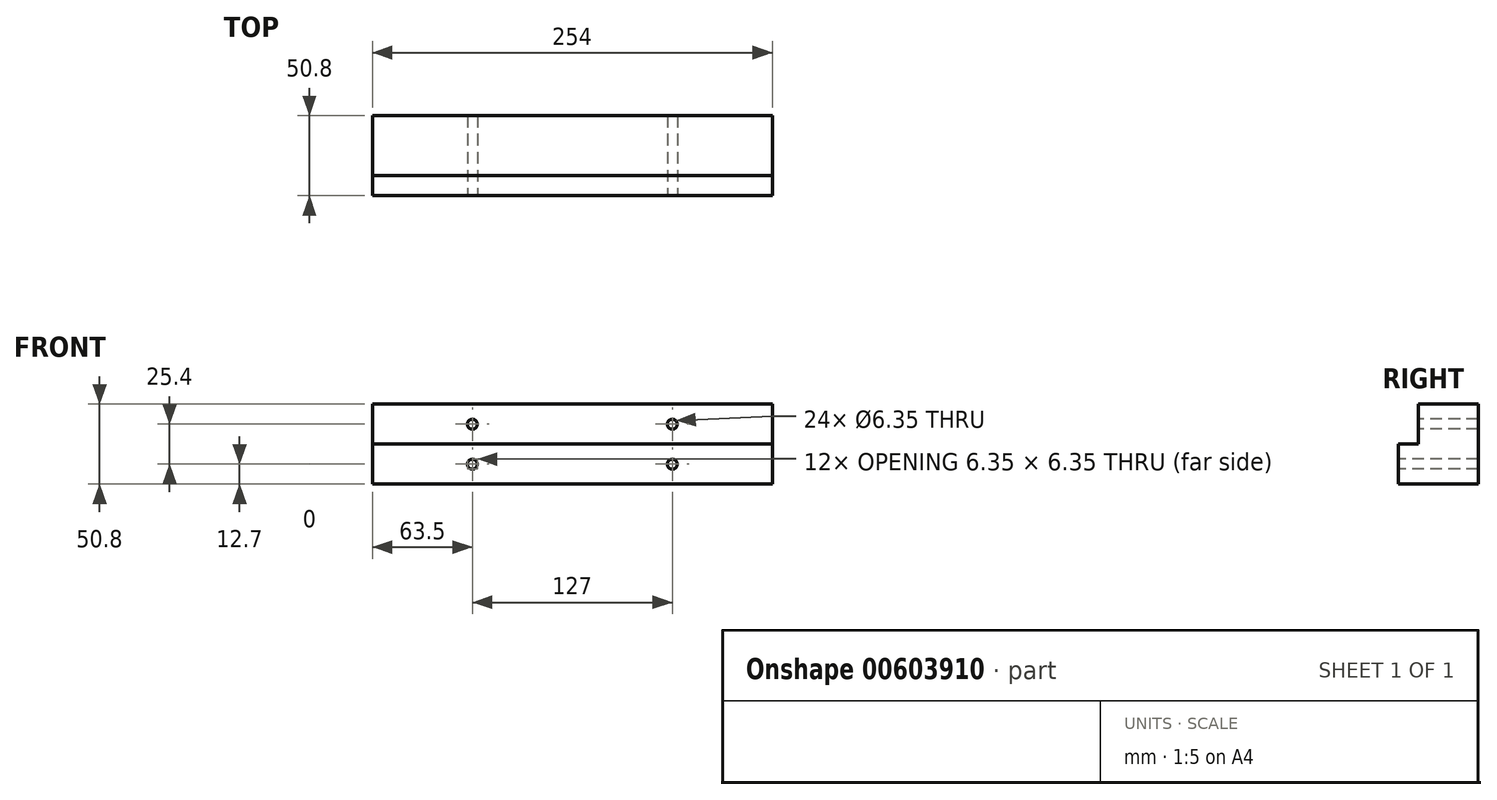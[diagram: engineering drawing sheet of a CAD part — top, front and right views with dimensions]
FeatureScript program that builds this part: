
annotation { "Feature Type Name" : "Feature", "Feature Type Description" : "" }
export const myFeature = defineFeature(function(context is Context, id is Id, definition is map)
    precondition{}
    {
        {
            var Q0;
            Q0=qCreatedBy(makeId("Right.planeOp"),FACE);
            var sketch = newSketch(context, id + "F0", { "sketchPlane" : qUnion([Q0])});
            skLineSegment(sketch, "E0", {"start": v(0, 0) * mm, "end": v(0, 25.4) * mm});
            skLineSegment(sketch, "E1", {"start": v(0, 25.4) * mm, "end": v(12.7, 25.4) * mm});
            skLineSegment(sketch, "E2", {"start": v(12.7, 25.4) * mm, "end": v(12.7, 50.8) * mm});
            skLineSegment(sketch, "E3", {"start": v(12.7, 50.8) * mm, "end": v(50.8, 50.8) * mm});
            skLineSegment(sketch, "E4", {"start": v(50.8, 50.8) * mm, "end": v(50.8, 0) * mm});
            skLineSegment(sketch, "E5", {"start": v(50.8, 0) * mm, "end": v(0, 0) * mm});
            skSolve(sketch);
        }
        {
            var Q0;
            Q0=makeQuery(id+"F0.imprint","IMPRINT",FACE,{"disambiguationData":[TD([[makeQuery(id+"F0.imprint","IMPRINT",EDGE,{"derivedFrom":sQuery(id+"F0.wireOp",EDGE,"E0")}),-1.0]])]});
            extrude(context, id + "F1", {"entities" : qUnion([Q0]), "depth" : 127 * mm, "offsetDistance" : 25.4 * mm, "hasSecondDirection" : true, "secondDirectionOppositeDirection" : true, "secondDirectionDepth" : 127 * mm});
        }
        {
            var Q0;
            Q0=makeQuery(id+"F1.opExtrude","SWEPT_FACE",FACE,{"disambiguationData":[OSD([sQuery(id+"F0.wireOp",EDGE,"E0")])]});
            var sketch = newSketch(context, id + "F2", { "sketchPlane" : qUnion([Q0])});
            skPoint(sketch, "E6", {"position": v(-63.5, 12.7) * mm});
            skPoint(sketch, "E6.positionSnap0", {"position": v(-127, 12.7) * mm});
            skPoint(sketch, "E7", {"position": v(63.5, 12.7) * mm});
            skPoint(sketch, "E7.positionSnap0", {"position": v(127, 12.7) * mm});
            skSolve(sketch);
        }
        {
            var Q0;
            Q0=makeQuery(id+"F1.opExtrude","SWEPT_FACE",FACE,{"disambiguationData":[OSD([sQuery(id+"F0.wireOp",EDGE,"E2")])]});
            var sketch = newSketch(context, id + "F3", { "sketchPlane" : qUnion([Q0])});
            skPoint(sketch, "E8", {"position": v(-63.5, 38.1) * mm});
            skPoint(sketch, "E8.positionSnap0", {"position": v(-127, 38.1) * mm});
            skPoint(sketch, "E9", {"position": v(63.5, 38.1) * mm});
            skPoint(sketch, "E9.positionSnap0", {"position": v(127, 38.1) * mm});
            skSolve(sketch);
        }
        {
            var Q0;
            Q0=sQuery(id+"F3.wireOp",VERTEX,"E8");
            var Q1;
            Q1=sQuery(id+"F2.wireOp",VERTEX,"E6");
            var Q2;
            Q2=sQuery(id+"F3.wireOp",VERTEX,"E9");
            var Q3;
            Q3=sQuery(id+"F2.wireOp",VERTEX,"E7");
            var Q4;
            Q4=makeQuery(id+"F1.opExtrude","SWEPT_BODY",BODY,{"disambiguationData":[OSD([sQuery(id+"F0.wireOp",EDGE,"E0"),sQuery(id+"F0.wireOp",EDGE,"E1"),sQuery(id+"F0.wireOp",EDGE,"E2"),sQuery(id+"F0.wireOp",EDGE,"E3"),sQuery(id+"F0.wireOp",EDGE,"E4"),sQuery(id+"F0.wireOp",EDGE,"E5")])]});
            hole(context, id + "F4", {"style" : HoleStyle.SIMPLE, "endStyle" : HoleEndStyle.THROUGH, "holeDiameter" : 6.35 * mm, "majorDiameter" : 6.35 * mm, "isTappedThrough" : true, "tappedDepth" : 12.7 * mm, "tapClearance" : 3, "startFromSketch" : true, "locations" : qUnion([Q0, Q1, Q2, Q3]), "scope" : qUnion([Q4])});
        }
    });
